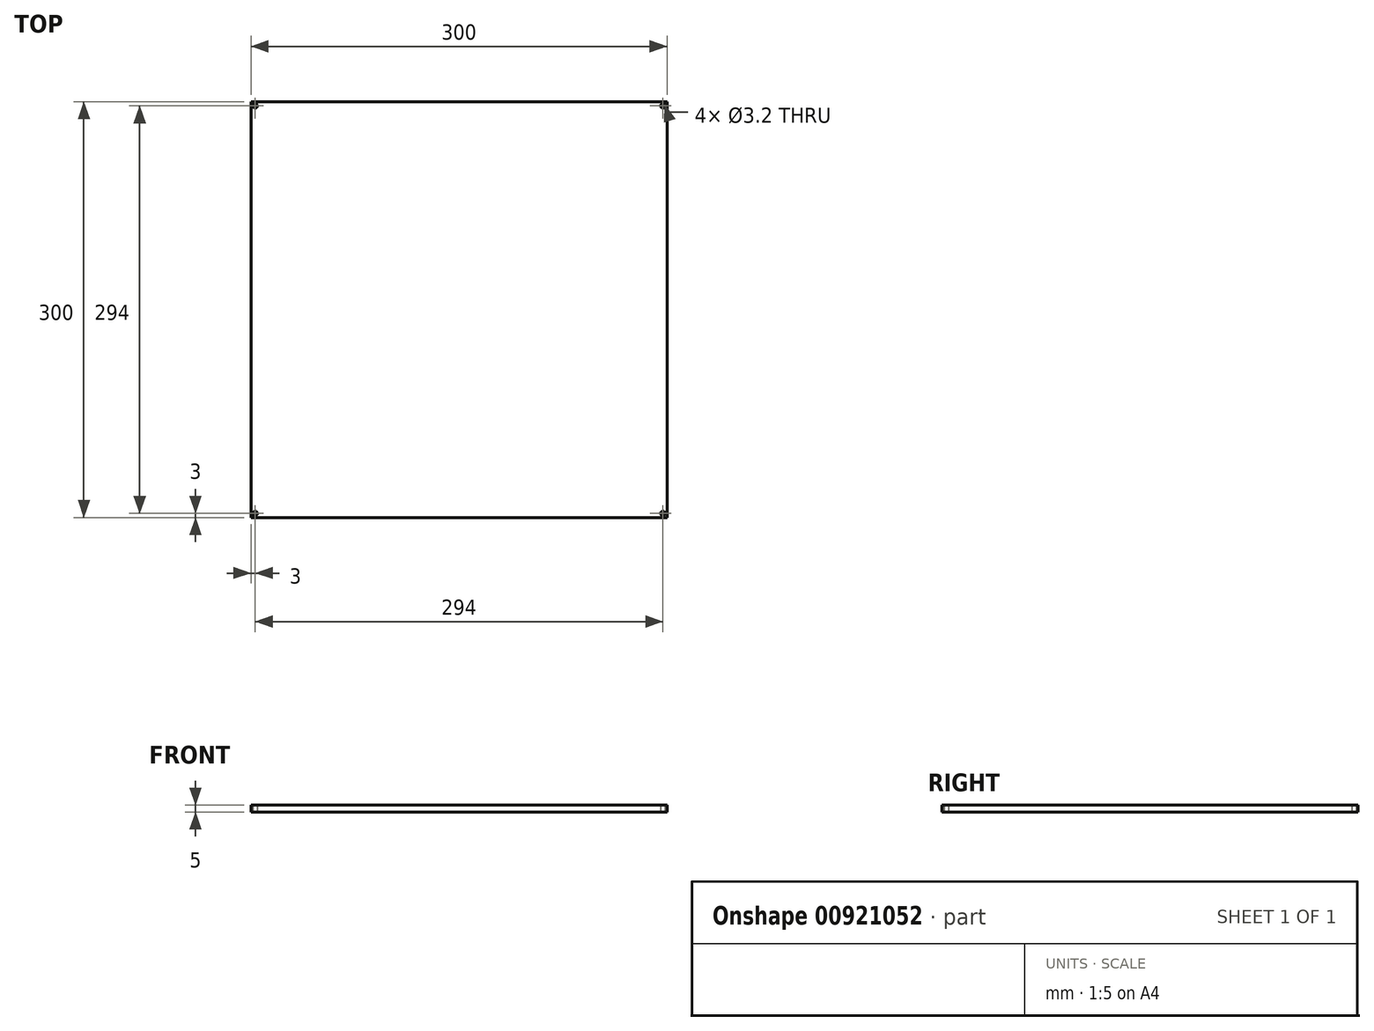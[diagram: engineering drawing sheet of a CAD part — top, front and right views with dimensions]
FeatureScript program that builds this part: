
annotation { "Feature Type Name" : "Feature", "Feature Type Description" : "" }
export const myFeature = defineFeature(function(context is Context, id is Id, definition is map)
    precondition{}
    {
        {
            var Q0;
            Q0=qCreatedBy(makeId("Top.planeOp"),FACE);
            var sketch = newSketch(context, id + "F0", { "sketchPlane" : qUnion([Q0])});
            skLineSegment(sketch, "E0.bottom", {"start": v(0, 0) * mm, "end": v(330, 0) * mm});
            skLineSegment(sketch, "E0.top", {"start": v(0, -330) * mm, "end": v(330, -330) * mm});
            skLineSegment(sketch, "E0.left", {"start": v(0, 0) * mm, "end": v(0, -330) * mm});
            skLineSegment(sketch, "E0.right", {"start": v(330, 0) * mm, "end": v(330, -330) * mm});
            skLineSegment(sketch, "E1.bottom", {"start": v(15, -15) * mm, "end": v(315, -15) * mm});
            skLineSegment(sketch, "E1.top", {"start": v(15, -315) * mm, "end": v(315, -315) * mm});
            skLineSegment(sketch, "E1.left", {"start": v(15, -15) * mm, "end": v(15, -315) * mm});
            skLineSegment(sketch, "E1.right", {"start": v(315, -15) * mm, "end": v(315, -315) * mm});
            skSolve(sketch);
        }
        {
            var Q0;
            Q0=makeQuery(id+"F0.imprint","IMPRINT",FACE,{"disambiguationData":[TD([[makeQuery(id+"F0.imprint","IMPRINT",EDGE,{"derivedFrom":sQuery(id+"F0.wireOp",EDGE,"E1.bottom")}),-1.0]])]});
            extrude(context, id + "F1", {"entities" : qUnion([Q0]), "depth" : 5 * mm, "offsetDistance" : 25 * mm});
        }
        {
            var Q0;
            Q0=makeQuery(id+"F1.opExtrude","CAP_FACE",FACE,{"disambiguationData":[OSD([sQuery(id+"F0.wireOp",EDGE,"E1.bottom"),sQuery(id+"F0.wireOp",EDGE,"E1.top"),sQuery(id+"F0.wireOp",EDGE,"E1.left"),sQuery(id+"F0.wireOp",EDGE,"E1.right")])],"isStart":false});
            var sketch = newSketch(context, id + "F2", { "sketchPlane" : qUnion([Q0])});
            skPoint(sketch, "E2", {"position": v(18, -18) * mm});
            skPoint(sketch, "E3", {"position": v(312, -18) * mm});
            skPoint(sketch, "E4", {"position": v(312, -312) * mm});
            skPoint(sketch, "E5", {"position": v(18, -312) * mm});
            skLineSegment(sketch, "E6", {"start": v(18, -18) * mm, "end": v(18, -15) * mm, "construction": true});
            skLineSegment(sketch, "E7", {"start": v(18, -18) * mm, "end": v(15, -18) * mm, "construction": true});
            skLineSegment(sketch, "E8", {"start": v(312, -18) * mm, "end": v(312, -15) * mm, "construction": true});
            skLineSegment(sketch, "E9", {"start": v(312, -18) * mm, "end": v(315, -18) * mm, "construction": true});
            skLineSegment(sketch, "E10", {"start": v(312, -312) * mm, "end": v(315, -312) * mm, "construction": true});
            skLineSegment(sketch, "E11", {"start": v(312, -312) * mm, "end": v(312, -315) * mm, "construction": true});
            skLineSegment(sketch, "E12", {"start": v(18, -312) * mm, "end": v(15, -312) * mm, "construction": true});
            skLineSegment(sketch, "E13", {"start": v(18, -312) * mm, "end": v(18, -315) * mm, "construction": true});
            skSolve(sketch);
        }
        {
            var Q0;
            Q0=sQuery(id+"F2.wireOp",VERTEX,"E2");
            var Q1;
            Q1=sQuery(id+"F2.wireOp",VERTEX,"E3");
            var Q2;
            Q2=sQuery(id+"F2.wireOp",VERTEX,"E4");
            var Q3;
            Q3=sQuery(id+"F2.wireOp",VERTEX,"E5");
            var Q4;
            Q4=makeQuery(id+"F1.opExtrude","SWEPT_BODY",BODY,{"disambiguationData":[OSD([sQuery(id+"F0.wireOp",EDGE,"E1.bottom"),sQuery(id+"F0.wireOp",EDGE,"E1.top"),sQuery(id+"F0.wireOp",EDGE,"E1.left"),sQuery(id+"F0.wireOp",EDGE,"E1.right")])]});
            hole(context, id + "F3", {"style" : HoleStyle.SIMPLE, "endStyle" : HoleEndStyle.THROUGH, "standardTappedOrClearance" : lookupTablePath({ "fit" : "Close", "standard" : "ISO", "size" : "M3", "type" : "Clearance" }), "standardBlindInLast" : lookupTablePath({ "fit" : "Close", "standard" : "ISO", "size" : "M3", "type" : "Clearance" }), "holeDiameter" : 3.2 * mm, "majorDiameter" : 5 * mm, "tappedDepth" : 5.3 * mm, "tapClearance" : 3, "locations" : qUnion([Q0, Q1, Q2, Q3]), "scope" : qUnion([Q4])});
        }
    });
